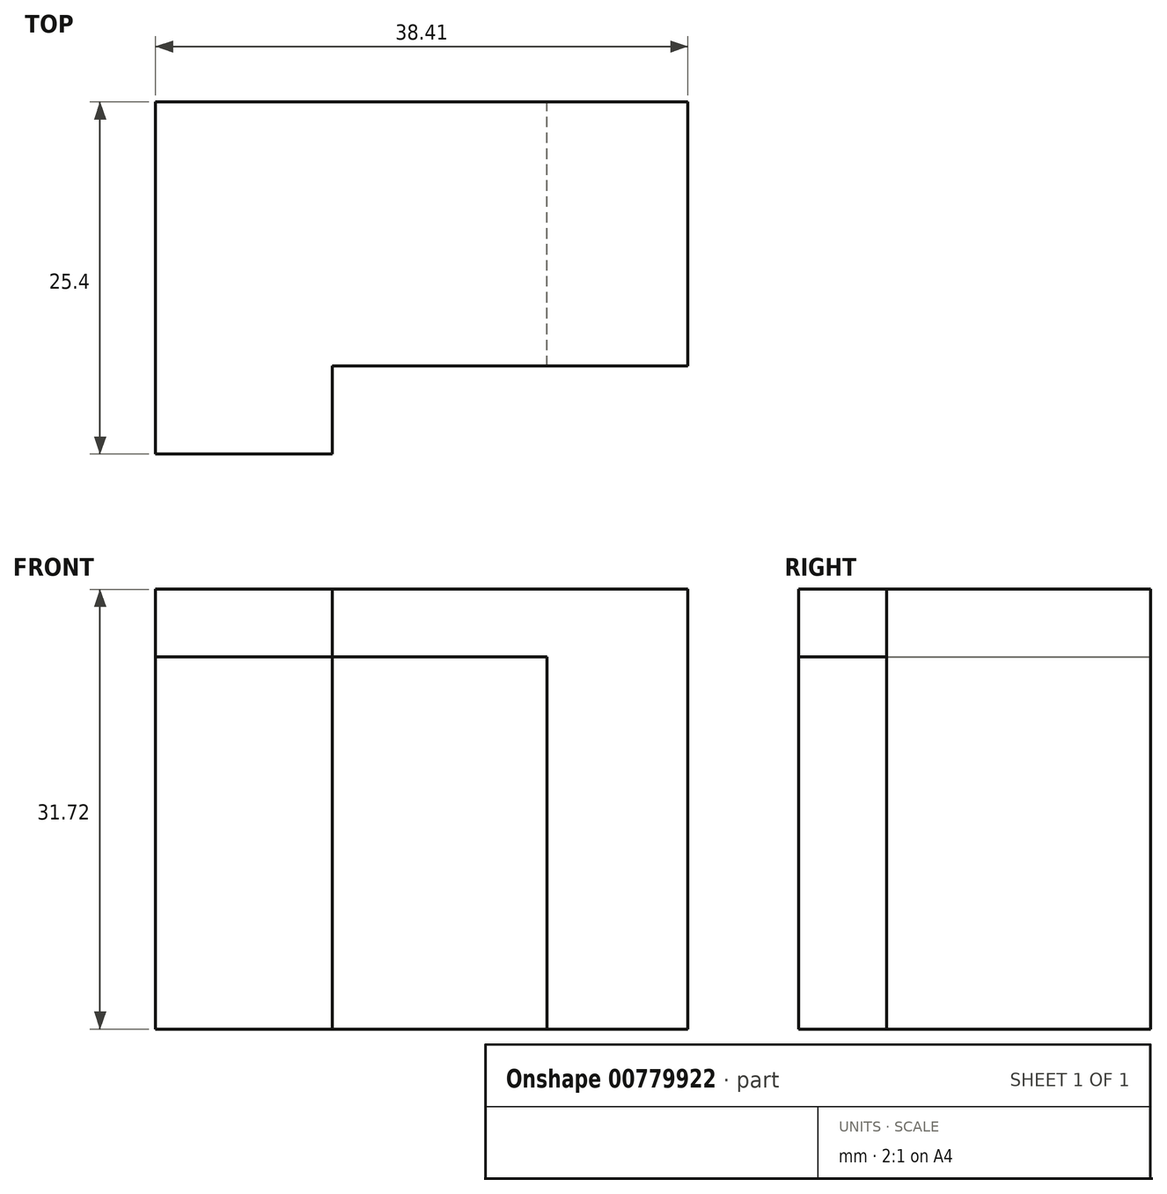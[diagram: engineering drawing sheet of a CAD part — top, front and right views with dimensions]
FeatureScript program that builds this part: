
annotation { "Feature Type Name" : "Feature", "Feature Type Description" : "" }
export const myFeature = defineFeature(function(context is Context, id is Id, definition is map)
    precondition{}
    {
        {
            var Q0;
            Q0=qCreatedBy(makeId("Front.planeOp"),FACE);
            var sketch = newSketch(context, id + "F0", { "sketchPlane" : qUnion([Q0])});
            skLineSegment(sketch, "E0", {"start": v(0, 0) * mm, "end": v(0, 26.84) * mm});
            skLineSegment(sketch, "E1", {"start": v(0, 26.84) * mm, "end": v(28.24, 26.84) * mm});
            skLineSegment(sketch, "E2", {"start": v(28.24, 26.84) * mm, "end": v(28.24, 0) * mm});
            skLineSegment(sketch, "E3", {"start": v(28.24, 0) * mm, "end": v(0, 0) * mm});
            skSolve(sketch);
        }
        {
            var Q0;
            Q0=qCreatedBy(makeId("Front.planeOp"),FACE);
            var sketch = newSketch(context, id + "F1", { "sketchPlane" : qUnion([Q0])});
            skLineSegment(sketch, "E4", {"start": v(0, 0) * mm, "end": v(38.41, 0) * mm});
            skLineSegment(sketch, "E5", {"start": v(0, 0) * mm, "end": v(0, 31.72) * mm});
            skLineSegment(sketch, "E6", {"start": v(0, 31.72) * mm, "end": v(39.22, 31.72) * mm});
            skLineSegment(sketch, "E7", {"start": v(38.41, 0) * mm, "end": v(38.41, 31.72) * mm});
            skSolve(sketch);
        }
        {
            var Q0;
            Q0=makeQuery(id+"F0.imprint","IMPRINT",FACE,{"disambiguationData":[TD([[makeQuery(id+"F0.imprint","IMPRINT",EDGE,{"derivedFrom":sQuery(id+"F0.wireOp",EDGE,"E0")}),-1.0]])]});
            extrude(context, id + "F2", {"entities" : qUnion([Q0]), "depth" : 25.4 * mm, "offsetDistance" : 25.4 * mm});
        }
        {
            var Q0;
            Q0 = qSketchRegion(id + "F1", true);
            extrude(context, id + "F3", {"entities" : qUnion([Q0]), "depth" : 25.4 * mm, "offsetDistance" : 25.4 * mm});
        }
        {
            var Q0;
            Q0=makeQuery(id+"F3.opExtrude","CAP_FACE",FACE,{"disambiguationData":[OSD([sQuery(id+"F1.wireOp",EDGE,"E4"),sQuery(id+"F1.wireOp",EDGE,"E5"),sQuery(id+"F1.wireOp",EDGE,"E6"),sQuery(id+"F1.wireOp",EDGE,"E7")])],"isStart":false});
            var sketch = newSketch(context, id + "F4", { "sketchPlane" : qUnion([Q0])});
            skLineSegment(sketch, "E8", {"start": v(0, 31.72) * mm, "end": v(12.77, 31.72) * mm});
            skLineSegment(sketch, "E9", {"start": v(12.77, 31.72) * mm, "end": v(12.77, 0) * mm});
            skSolve(sketch);
        }
        {
            var Q0;
            {var subQ0=sQuery(id+"F4.wireOp",EDGE,"E9");Q0=makeQuery(id+"F4.imprint","IMPRINT",FACE,{"disambiguationData":[TD([[makeQuery(id+"F4.imprint","IMPRINT",EDGE,{"derivedFrom":subQ0}),1.0]])]});}
            extrude(context, id + "F5", {"entities" : qUnion([Q0]), "operationType" : NewBodyOperationType.REMOVE, "oppositeDirection" : true, "depth" : 6.35 * mm, "offsetDistance" : 25.4 * mm});
        }
    });
